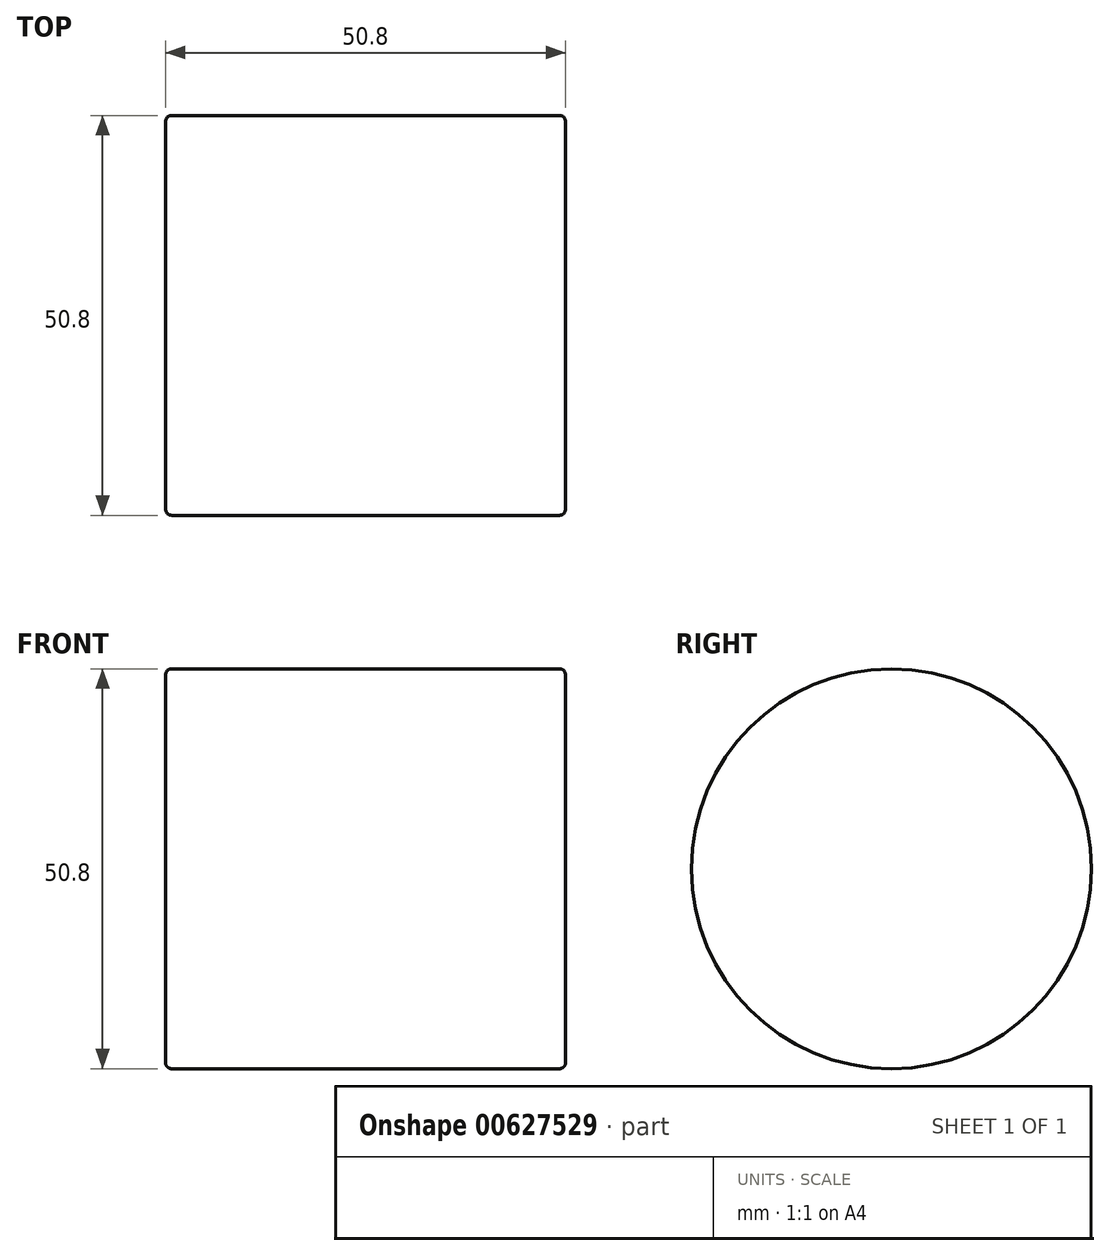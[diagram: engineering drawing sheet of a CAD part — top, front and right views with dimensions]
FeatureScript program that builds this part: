
annotation { "Feature Type Name" : "Feature", "Feature Type Description" : "" }
export const myFeature = defineFeature(function(context is Context, id is Id, definition is map)
    precondition{}
    {
        {
            var Q0;
            Q0=qCreatedBy(makeId("Right.planeOp"),FACE);
            var sketch = newSketch(context, id + "F0", { "sketchPlane" : qUnion([Q0])});
            skCircle(sketch, "E0", {"center": v(0, 0) * mm, "radius": 25.4 * mm});
            skSolve(sketch);
        }
        {
            var Q0;
            Q0=qSketchRegion(id+"F0",true);
            extrude(context, id + "F1", {"entities" : qUnion([Q0]), "endBound" : BoundingType.SYMMETRIC, "depth" : 50.8 * mm, "offsetDistance" : 25.4 * mm});
        }
        {
            var Q0;
            Q0=makeQuery(id+"F1.opExtrude","CAP_EDGE",EDGE,{"disambiguationData":[OSD([sQuery(id+"F0.wireOp",EDGE,"E0")])],"isStart":false});
            var Q1;
            Q1=makeQuery(id+"F1.opExtrude","CAP_EDGE",EDGE,{"disambiguationData":[OSD([sQuery(id+"F0.wireOp",EDGE,"E0")])],"isStart":true});
            fillet(context, id + "F2", {"entities" : qUnion([Q0, Q1]), "radius" : 0.76 * mm, "tangentPropagation" : true, "allowEdgeOverflow" : false});
        }
    });
